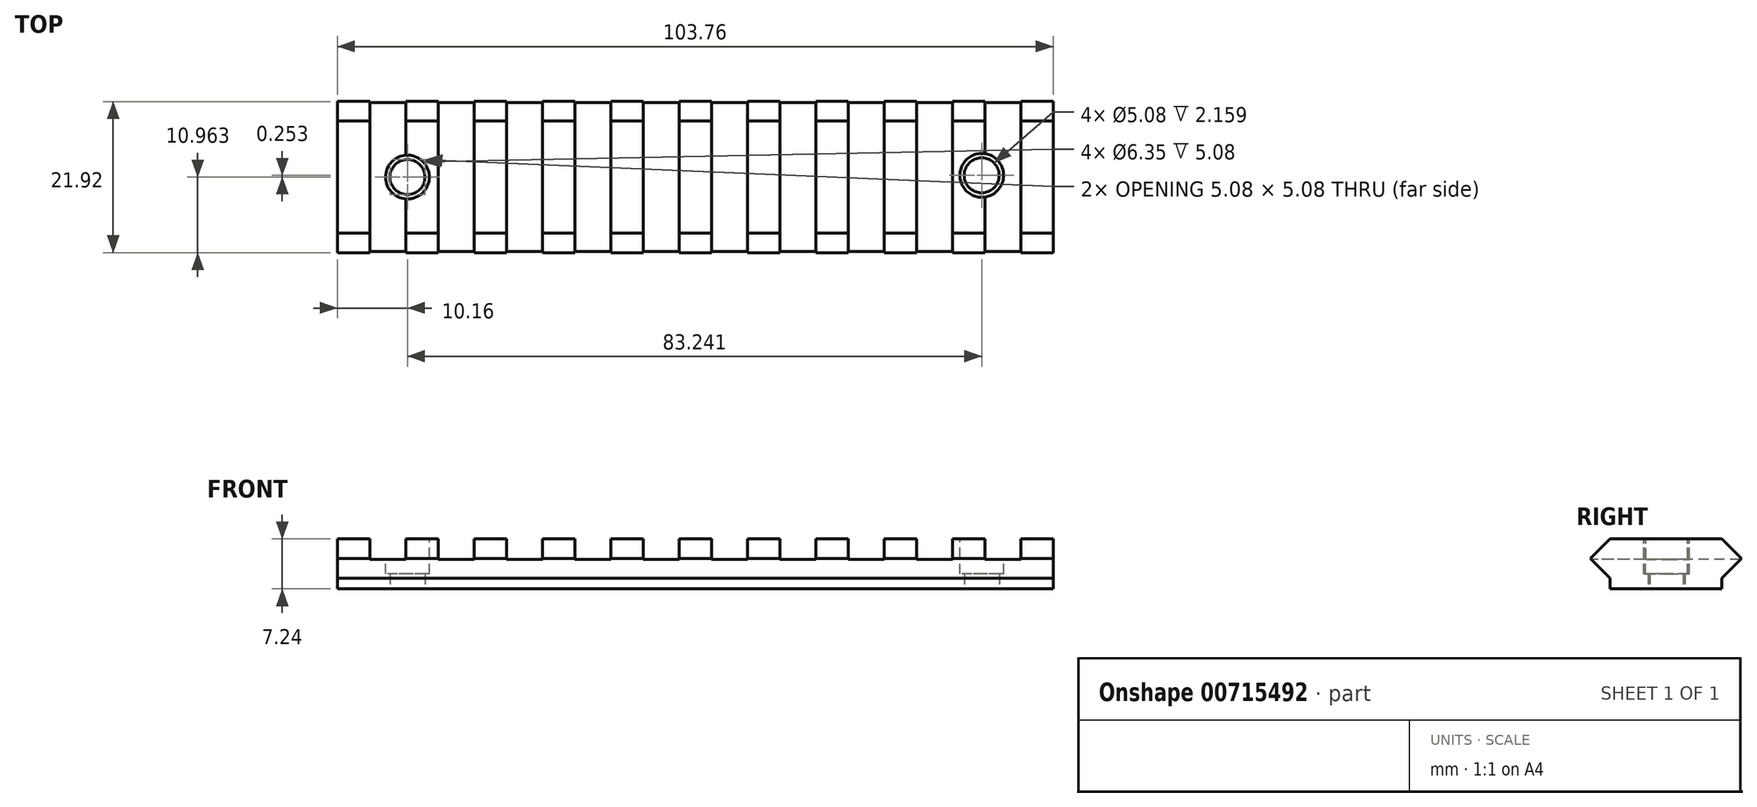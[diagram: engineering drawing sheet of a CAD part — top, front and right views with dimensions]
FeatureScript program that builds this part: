
annotation { "Feature Type Name" : "Feature", "Feature Type Description" : "" }
export const myFeature = defineFeature(function(context is Context, id is Id, definition is map)
    precondition{}
    {
        {
            var Q0;
            Q0=qCreatedBy(makeId("Right.planeOp"),FACE);
            var sketch = newSketch(context, id + "F0", { "sketchPlane" : qUnion([Q0])});
            skLineSegment(sketch, "E0", {"start": v(0, 0) * mm, "end": v(0, 1.52) * mm});
            skLineSegment(sketch, "E1", {"start": v(0, 1.52) * mm, "end": v(-2.86, 4.38) * mm});
            skLineSegment(sketch, "E2", {"start": v(-2.86, 4.38) * mm, "end": v(0, 7.24) * mm});
            skLineSegment(sketch, "E3", {"start": v(0, 7.24) * mm, "end": v(16.2, 7.24) * mm});
            skLineSegment(sketch, "E4", {"start": v(0, 0) * mm, "end": v(16.2, 0) * mm});
            skLineSegment(sketch, "E5", {"start": v(16.2, 0) * mm, "end": v(16.2, 1.52) * mm});
            skLineSegment(sketch, "E6", {"start": v(16.2, 1.52) * mm, "end": v(19.06, 4.38) * mm});
            skLineSegment(sketch, "E7", {"start": v(19.06, 4.38) * mm, "end": v(16.2, 7.24) * mm});
            skSolve(sketch);
        }
        {
            var Q0;
            Q0=makeQuery(id+"F0.imprint","IMPRINT",FACE,{"disambiguationData":[TD([[makeQuery(id+"F0.imprint","IMPRINT",EDGE,{"derivedFrom":sQuery(id+"F0.wireOp",EDGE,"E0")}),-1.0]])]});
            extrude(context, id + "F1", {"entities" : qUnion([Q0]), "depth" : 103.76 * mm});
        }
        {
            var Q0;
            Q0=makeQuery(id+"F1.opExtrude","SWEPT_FACE",FACE,{"disambiguationData":[OSD([sQuery(id+"F0.wireOp",EDGE,"E3")])]});
            var sketch = newSketch(context, id + "F2", { "sketchPlane" : qUnion([Q0])});
            skLineSegment(sketch, "E8", {"start": v(0, 8.1) * mm, "end": v(4.7, 8.1) * mm, "construction": true});
            skLineSegment(sketch, "E9", {"start": v(4.7, 8.1) * mm, "end": v(4.7, 19.06) * mm});
            skLineSegment(sketch, "E10", {"start": v(4.7, 8.1) * mm, "end": v(4.7, -2.86) * mm});
            skLineSegment(sketch, "E11", {"start": v(4.7, 8.1) * mm, "end": v(9.9, 8.1) * mm, "construction": true});
            skLineSegment(sketch, "E12", {"start": v(4.7, 19.06) * mm, "end": v(9.9, 19.06) * mm});
            skLineSegment(sketch, "E13", {"start": v(9.9, 19.06) * mm, "end": v(9.9, -2.86) * mm});
            skLineSegment(sketch, "E14", {"start": v(4.7, -2.86) * mm, "end": v(9.9, -2.86) * mm});
            skLineSegment(sketch, "E15", {"start": v(9.9, 8.1) * mm, "end": v(14.6, 8.1) * mm, "construction": true});
            skLineSegment(sketch, "E16.bottom", {"start": v(14.6, 19.06) * mm, "end": v(19.81, 19.06) * mm});
            skLineSegment(sketch, "E16.top", {"start": v(14.6, -2.86) * mm, "end": v(19.81, -2.86) * mm});
            skLineSegment(sketch, "E16.left", {"start": v(14.6, 19.06) * mm, "end": v(14.6, -2.86) * mm});
            skLineSegment(sketch, "E16.right", {"start": v(19.81, 19.06) * mm, "end": v(19.81, -2.86) * mm});
            skLineSegment(sketch, "E17", {"start": v(19.81, 8.1) * mm, "end": v(24.51, 8.1) * mm, "construction": true});
            skLineSegment(sketch, "E18.bottom", {"start": v(24.51, 19.06) * mm, "end": v(29.72, 19.06) * mm});
            skLineSegment(sketch, "E18.top", {"start": v(24.51, -2.86) * mm, "end": v(29.72, -2.86) * mm});
            skLineSegment(sketch, "E18.left", {"start": v(24.51, 19.06) * mm, "end": v(24.51, -2.86) * mm});
            skLineSegment(sketch, "E18.right", {"start": v(29.72, 19.06) * mm, "end": v(29.72, -2.86) * mm});
            skLineSegment(sketch, "E19.bottom", {"start": v(34.42, 19.06) * mm, "end": v(39.62, 19.06) * mm});
            skLineSegment(sketch, "E19.top", {"start": v(34.42, -2.86) * mm, "end": v(39.62, -2.86) * mm});
            skLineSegment(sketch, "E19.left", {"start": v(34.42, 19.06) * mm, "end": v(34.42, -2.86) * mm});
            skLineSegment(sketch, "E19.right", {"start": v(39.62, 19.06) * mm, "end": v(39.62, -2.86) * mm});
            skLineSegment(sketch, "E20", {"start": v(39.62, 8.1) * mm, "end": v(44.32, 8.1) * mm, "construction": true});
            skLineSegment(sketch, "E21.bottom", {"start": v(44.32, 19.06) * mm, "end": v(49.53, 19.06) * mm});
            skLineSegment(sketch, "E21.top", {"start": v(44.32, -2.86) * mm, "end": v(49.53, -2.86) * mm});
            skLineSegment(sketch, "E21.left", {"start": v(44.32, 19.06) * mm, "end": v(44.32, -2.86) * mm});
            skLineSegment(sketch, "E21.right", {"start": v(49.53, 19.06) * mm, "end": v(49.53, -2.86) * mm});
            skLineSegment(sketch, "E22", {"start": v(49.53, 8.1) * mm, "end": v(54.23, 8.1) * mm, "construction": true});
            skLineSegment(sketch, "E23.bottom", {"start": v(54.23, 19.06) * mm, "end": v(59.44, 19.06) * mm});
            skLineSegment(sketch, "E23.top", {"start": v(54.23, -2.86) * mm, "end": v(59.44, -2.86) * mm});
            skLineSegment(sketch, "E23.left", {"start": v(54.23, 19.06) * mm, "end": v(54.23, -2.86) * mm});
            skLineSegment(sketch, "E23.right", {"start": v(59.44, 19.06) * mm, "end": v(59.44, -2.86) * mm});
            skLineSegment(sketch, "E24", {"start": v(59.44, 8.1) * mm, "end": v(64.13, 8.1) * mm, "construction": true});
            skLineSegment(sketch, "E25.bottom", {"start": v(64.13, 19.06) * mm, "end": v(69.34, 19.06) * mm});
            skLineSegment(sketch, "E25.top", {"start": v(64.13, -2.86) * mm, "end": v(69.34, -2.86) * mm});
            skLineSegment(sketch, "E25.left", {"start": v(64.13, 19.06) * mm, "end": v(64.13, -2.86) * mm});
            skLineSegment(sketch, "E25.right", {"start": v(69.34, 19.06) * mm, "end": v(69.34, -2.86) * mm});
            skLineSegment(sketch, "E26", {"start": v(69.34, 8.1) * mm, "end": v(74.04, 8.1) * mm, "construction": true});
            skLineSegment(sketch, "E27", {"start": v(29.72, 8.1) * mm, "end": v(34.42, 8.1) * mm, "construction": true});
            skLineSegment(sketch, "E28.bottom", {"start": v(74.04, 19.06) * mm, "end": v(79.25, 19.06) * mm});
            skLineSegment(sketch, "E28.top", {"start": v(74.04, -2.86) * mm, "end": v(79.25, -2.86) * mm});
            skLineSegment(sketch, "E28.left", {"start": v(74.04, 19.06) * mm, "end": v(74.04, -2.86) * mm});
            skLineSegment(sketch, "E28.right", {"start": v(79.25, 19.06) * mm, "end": v(79.25, -2.86) * mm});
            skLineSegment(sketch, "E29", {"start": v(79.25, 8.1) * mm, "end": v(83.95, 8.1) * mm, "construction": true});
            skLineSegment(sketch, "E30.bottom", {"start": v(83.95, 19.06) * mm, "end": v(89.15, 19.06) * mm});
            skLineSegment(sketch, "E30.top", {"start": v(83.95, -2.86) * mm, "end": v(89.15, -2.86) * mm});
            skLineSegment(sketch, "E30.left", {"start": v(83.95, 19.06) * mm, "end": v(83.95, -2.86) * mm});
            skLineSegment(sketch, "E30.right", {"start": v(89.15, 19.06) * mm, "end": v(89.15, -2.86) * mm});
            skLineSegment(sketch, "E31", {"start": v(89.15, 8.1) * mm, "end": v(93.85, 8.1) * mm, "construction": true});
            skLineSegment(sketch, "E32.bottom", {"start": v(93.85, 19.15) * mm, "end": v(99.06, 19.15) * mm});
            skLineSegment(sketch, "E32.top", {"start": v(93.85, -2.94) * mm, "end": v(99.06, -2.94) * mm});
            skLineSegment(sketch, "E32.left", {"start": v(93.85, 19.15) * mm, "end": v(93.85, -2.94) * mm});
            skLineSegment(sketch, "E32.right", {"start": v(99.06, 19.15) * mm, "end": v(99.06, -2.94) * mm});
            skSolve(sketch);
        }
        {
            var Q0;
            {var subQ0=sQuery(id+"F2.wireOp",EDGE,"E14");Q0=makeQuery(id+"F2.imprint","IMPRINT",FACE,{"disambiguationData":[TD([[makeQuery(id+"F2.imprint","IMPRINT",EDGE,{"derivedFrom":subQ0}),1.0]])]});}
            var Q1;
            {var subQ0=sQuery(id+"F2.wireOp",EDGE,"E10");var subQ8=sQuery(id+"F2.wireOp",EDGE,"E9");var subQ9=makeQuery(id+"F2.imprint","INTERSECT",VERTEX,{"derivedFrom":[subQ8,subQ0]});Q1=makeQuery(id+"F2.imprint","IMPRINT",FACE,{"disambiguationData":[TD([[makeQuery(id+"F2.imprint","IMPRINT",EDGE,{"disambiguationData":[TD([[subQ9,-1.0]])],"derivedFrom":subQ8}),-1.0]])]});}
            var Q2;
            {var subQ0=sQuery(id+"F2.wireOp",EDGE,"E12");Q2=makeQuery(id+"F2.imprint","IMPRINT",FACE,{"disambiguationData":[TD([[makeQuery(id+"F2.imprint","IMPRINT",EDGE,{"derivedFrom":subQ0}),-1.0]])]});}
            var Q3;
            {var subQ0=sQuery(id+"F2.wireOp",EDGE,"E16.bottom");Q3=makeQuery(id+"F2.imprint","IMPRINT",FACE,{"disambiguationData":[TD([[makeQuery(id+"F2.imprint","IMPRINT",EDGE,{"derivedFrom":subQ0}),-1.0]])]});}
            var Q4;
            {var subQ0=sQuery(id+"F2.wireOp",EDGE,"E16.left");var subQ1=sQuery(id+"F0.wireOp",EDGE,"E3");var subQ2=makeQuery(id+"F1.opExtrude","SWEPT_EDGE",EDGE,{"disambiguationData":[OSD([subQ1,sQuery(id+"F0.wireOp",EDGE,"E7")])]});var subQ3=makeQuery(id+"F2.imprint","INTERSECT",VERTEX,{"derivedFrom":[subQ2,subQ0]});Q4=makeQuery(id+"F2.imprint","IMPRINT",FACE,{"disambiguationData":[TD([[makeQuery(id+"F2.imprint","IMPRINT",EDGE,{"disambiguationData":[TD([[subQ3,-1.0]])],"derivedFrom":subQ0}),1.0]])]});}
            var Q5;
            {var subQ0=sQuery(id+"F2.wireOp",EDGE,"E16.top");Q5=makeQuery(id+"F2.imprint","IMPRINT",FACE,{"disambiguationData":[TD([[makeQuery(id+"F2.imprint","IMPRINT",EDGE,{"derivedFrom":subQ0}),1.0]])]});}
            var Q6;
            {var subQ0=sQuery(id+"F2.wireOp",EDGE,"E18.bottom");Q6=makeQuery(id+"F2.imprint","IMPRINT",FACE,{"disambiguationData":[TD([[makeQuery(id+"F2.imprint","IMPRINT",EDGE,{"derivedFrom":subQ0}),-1.0]])]});}
            var Q7;
            {var subQ0=sQuery(id+"F2.wireOp",EDGE,"E18.left");var subQ1=sQuery(id+"F0.wireOp",EDGE,"E3");var subQ2=makeQuery(id+"F1.opExtrude","SWEPT_EDGE",EDGE,{"disambiguationData":[OSD([subQ1,sQuery(id+"F0.wireOp",EDGE,"E7")])]});var subQ3=makeQuery(id+"F2.imprint","INTERSECT",VERTEX,{"derivedFrom":[subQ2,subQ0]});Q7=makeQuery(id+"F2.imprint","IMPRINT",FACE,{"disambiguationData":[TD([[makeQuery(id+"F2.imprint","IMPRINT",EDGE,{"disambiguationData":[TD([[subQ3,-1.0]])],"derivedFrom":subQ0}),1.0]])]});}
            var Q8;
            {var subQ0=sQuery(id+"F2.wireOp",EDGE,"E18.top");Q8=makeQuery(id+"F2.imprint","IMPRINT",FACE,{"disambiguationData":[TD([[makeQuery(id+"F2.imprint","IMPRINT",EDGE,{"derivedFrom":subQ0}),1.0]])]});}
            var Q9;
            {var subQ0=sQuery(id+"F2.wireOp",EDGE,"E19.bottom");Q9=makeQuery(id+"F2.imprint","IMPRINT",FACE,{"disambiguationData":[TD([[makeQuery(id+"F2.imprint","IMPRINT",EDGE,{"derivedFrom":subQ0}),-1.0]])]});}
            var Q10;
            {var subQ0=sQuery(id+"F2.wireOp",EDGE,"E19.left");var subQ1=sQuery(id+"F0.wireOp",EDGE,"E3");var subQ2=makeQuery(id+"F1.opExtrude","SWEPT_EDGE",EDGE,{"disambiguationData":[OSD([subQ1,sQuery(id+"F0.wireOp",EDGE,"E7")])]});var subQ3=makeQuery(id+"F2.imprint","INTERSECT",VERTEX,{"derivedFrom":[subQ2,subQ0]});Q10=makeQuery(id+"F2.imprint","IMPRINT",FACE,{"disambiguationData":[TD([[makeQuery(id+"F2.imprint","IMPRINT",EDGE,{"disambiguationData":[TD([[subQ3,-1.0]])],"derivedFrom":subQ0}),1.0]])]});}
            var Q11;
            {var subQ0=sQuery(id+"F2.wireOp",EDGE,"E19.top");Q11=makeQuery(id+"F2.imprint","IMPRINT",FACE,{"disambiguationData":[TD([[makeQuery(id+"F2.imprint","IMPRINT",EDGE,{"derivedFrom":subQ0}),1.0]])]});}
            var Q12;
            {var subQ0=sQuery(id+"F2.wireOp",EDGE,"E21.bottom");Q12=makeQuery(id+"F2.imprint","IMPRINT",FACE,{"disambiguationData":[TD([[makeQuery(id+"F2.imprint","IMPRINT",EDGE,{"derivedFrom":subQ0}),-1.0]])]});}
            var Q13;
            {var subQ0=sQuery(id+"F2.wireOp",EDGE,"E21.left");var subQ1=sQuery(id+"F0.wireOp",EDGE,"E3");var subQ2=makeQuery(id+"F1.opExtrude","SWEPT_EDGE",EDGE,{"disambiguationData":[OSD([subQ1,sQuery(id+"F0.wireOp",EDGE,"E7")])]});var subQ3=makeQuery(id+"F2.imprint","INTERSECT",VERTEX,{"derivedFrom":[subQ2,subQ0]});Q13=makeQuery(id+"F2.imprint","IMPRINT",FACE,{"disambiguationData":[TD([[makeQuery(id+"F2.imprint","IMPRINT",EDGE,{"disambiguationData":[TD([[subQ3,-1.0]])],"derivedFrom":subQ0}),1.0]])]});}
            var Q14;
            {var subQ0=sQuery(id+"F2.wireOp",EDGE,"E21.top");Q14=makeQuery(id+"F2.imprint","IMPRINT",FACE,{"disambiguationData":[TD([[makeQuery(id+"F2.imprint","IMPRINT",EDGE,{"derivedFrom":subQ0}),1.0]])]});}
            var Q15;
            {var subQ0=sQuery(id+"F2.wireOp",EDGE,"E23.bottom");Q15=makeQuery(id+"F2.imprint","IMPRINT",FACE,{"disambiguationData":[TD([[makeQuery(id+"F2.imprint","IMPRINT",EDGE,{"derivedFrom":subQ0}),-1.0]])]});}
            var Q16;
            {var subQ0=sQuery(id+"F2.wireOp",EDGE,"E23.left");var subQ1=sQuery(id+"F0.wireOp",EDGE,"E3");var subQ2=makeQuery(id+"F1.opExtrude","SWEPT_EDGE",EDGE,{"disambiguationData":[OSD([subQ1,sQuery(id+"F0.wireOp",EDGE,"E7")])]});var subQ3=makeQuery(id+"F2.imprint","INTERSECT",VERTEX,{"derivedFrom":[subQ2,subQ0]});Q16=makeQuery(id+"F2.imprint","IMPRINT",FACE,{"disambiguationData":[TD([[makeQuery(id+"F2.imprint","IMPRINT",EDGE,{"disambiguationData":[TD([[subQ3,-1.0]])],"derivedFrom":subQ0}),1.0]])]});}
            var Q17;
            {var subQ0=sQuery(id+"F2.wireOp",EDGE,"E23.top");Q17=makeQuery(id+"F2.imprint","IMPRINT",FACE,{"disambiguationData":[TD([[makeQuery(id+"F2.imprint","IMPRINT",EDGE,{"derivedFrom":subQ0}),1.0]])]});}
            var Q18;
            {var subQ0=sQuery(id+"F2.wireOp",EDGE,"E25.bottom");Q18=makeQuery(id+"F2.imprint","IMPRINT",FACE,{"disambiguationData":[TD([[makeQuery(id+"F2.imprint","IMPRINT",EDGE,{"derivedFrom":subQ0}),-1.0]])]});}
            var Q19;
            {var subQ0=sQuery(id+"F2.wireOp",EDGE,"E25.left");var subQ1=sQuery(id+"F0.wireOp",EDGE,"E3");var subQ2=makeQuery(id+"F1.opExtrude","SWEPT_EDGE",EDGE,{"disambiguationData":[OSD([subQ1,sQuery(id+"F0.wireOp",EDGE,"E7")])]});var subQ3=makeQuery(id+"F2.imprint","INTERSECT",VERTEX,{"derivedFrom":[subQ2,subQ0]});Q19=makeQuery(id+"F2.imprint","IMPRINT",FACE,{"disambiguationData":[TD([[makeQuery(id+"F2.imprint","IMPRINT",EDGE,{"disambiguationData":[TD([[subQ3,-1.0]])],"derivedFrom":subQ0}),1.0]])]});}
            var Q20;
            {var subQ0=sQuery(id+"F2.wireOp",EDGE,"E25.top");Q20=makeQuery(id+"F2.imprint","IMPRINT",FACE,{"disambiguationData":[TD([[makeQuery(id+"F2.imprint","IMPRINT",EDGE,{"derivedFrom":subQ0}),1.0]])]});}
            var Q21;
            {var subQ0=sQuery(id+"F2.wireOp",EDGE,"E28.bottom");Q21=makeQuery(id+"F2.imprint","IMPRINT",FACE,{"disambiguationData":[TD([[makeQuery(id+"F2.imprint","IMPRINT",EDGE,{"derivedFrom":subQ0}),-1.0]])]});}
            var Q22;
            {var subQ0=sQuery(id+"F2.wireOp",EDGE,"E28.left");var subQ1=sQuery(id+"F0.wireOp",EDGE,"E3");var subQ2=makeQuery(id+"F1.opExtrude","SWEPT_EDGE",EDGE,{"disambiguationData":[OSD([subQ1,sQuery(id+"F0.wireOp",EDGE,"E7")])]});var subQ3=makeQuery(id+"F2.imprint","INTERSECT",VERTEX,{"derivedFrom":[subQ2,subQ0]});Q22=makeQuery(id+"F2.imprint","IMPRINT",FACE,{"disambiguationData":[TD([[makeQuery(id+"F2.imprint","IMPRINT",EDGE,{"disambiguationData":[TD([[subQ3,-1.0]])],"derivedFrom":subQ0}),1.0]])]});}
            var Q23;
            {var subQ0=sQuery(id+"F2.wireOp",EDGE,"E28.top");Q23=makeQuery(id+"F2.imprint","IMPRINT",FACE,{"disambiguationData":[TD([[makeQuery(id+"F2.imprint","IMPRINT",EDGE,{"derivedFrom":subQ0}),1.0]])]});}
            var Q24;
            {var subQ0=sQuery(id+"F2.wireOp",EDGE,"E30.top");Q24=makeQuery(id+"F2.imprint","IMPRINT",FACE,{"disambiguationData":[TD([[makeQuery(id+"F2.imprint","IMPRINT",EDGE,{"derivedFrom":subQ0}),1.0]])]});}
            var Q25;
            {var subQ0=sQuery(id+"F2.wireOp",EDGE,"E30.left");var subQ1=sQuery(id+"F0.wireOp",EDGE,"E3");var subQ2=makeQuery(id+"F1.opExtrude","SWEPT_EDGE",EDGE,{"disambiguationData":[OSD([subQ1,sQuery(id+"F0.wireOp",EDGE,"E7")])]});var subQ3=makeQuery(id+"F2.imprint","INTERSECT",VERTEX,{"derivedFrom":[subQ2,subQ0]});Q25=makeQuery(id+"F2.imprint","IMPRINT",FACE,{"disambiguationData":[TD([[makeQuery(id+"F2.imprint","IMPRINT",EDGE,{"disambiguationData":[TD([[subQ3,-1.0]])],"derivedFrom":subQ0}),1.0]])]});}
            var Q26;
            {var subQ0=sQuery(id+"F2.wireOp",EDGE,"E30.bottom");Q26=makeQuery(id+"F2.imprint","IMPRINT",FACE,{"disambiguationData":[TD([[makeQuery(id+"F2.imprint","IMPRINT",EDGE,{"derivedFrom":subQ0}),-1.0]])]});}
            var Q27;
            {var subQ0=sQuery(id+"F2.wireOp",EDGE,"E32.bottom");Q27=makeQuery(id+"F2.imprint","IMPRINT",FACE,{"disambiguationData":[TD([[makeQuery(id+"F2.imprint","IMPRINT",EDGE,{"derivedFrom":subQ0}),-1.0]])]});}
            var Q28;
            {var subQ0=sQuery(id+"F2.wireOp",EDGE,"E32.left");var subQ1=sQuery(id+"F0.wireOp",EDGE,"E3");var subQ2=makeQuery(id+"F1.opExtrude","SWEPT_EDGE",EDGE,{"disambiguationData":[OSD([subQ1,sQuery(id+"F0.wireOp",EDGE,"E7")])]});var subQ3=makeQuery(id+"F2.imprint","INTERSECT",VERTEX,{"derivedFrom":[subQ2,subQ0]});Q28=makeQuery(id+"F2.imprint","IMPRINT",FACE,{"disambiguationData":[TD([[makeQuery(id+"F2.imprint","IMPRINT",EDGE,{"disambiguationData":[TD([[subQ3,-1.0]])],"derivedFrom":subQ0}),1.0]])]});}
            var Q29;
            {var subQ0=sQuery(id+"F2.wireOp",EDGE,"E32.top");Q29=makeQuery(id+"F2.imprint","IMPRINT",FACE,{"disambiguationData":[TD([[makeQuery(id+"F2.imprint","IMPRINT",EDGE,{"derivedFrom":subQ0}),1.0]])]});}
            extrude(context, id + "F3", {"entities" : qUnion([Q0, Q1, Q2, Q3, Q4, Q5, Q6, Q7, Q8, Q9, Q10, Q11, Q12, Q13, Q14, Q15, Q16, Q17, Q18, Q19, Q20, Q21, Q22, Q23, Q24, Q25, Q26, Q27, Q28, Q29]), "operationType" : NewBodyOperationType.REMOVE, "oppositeDirection" : true, "depth" : 3 * mm});
        }
        {
            var Q0;
            Q0=makeQuery(id+"F1.opExtrude","SWEPT_FACE",FACE,{"disambiguationData":[OSD([sQuery(id+"F0.wireOp",EDGE,"E4")])]});
            var sketch = newSketch(context, id + "F4", { "sketchPlane" : qUnion([Q0])});
            skCircle(sketch, "E33", {"center": v(93.4, -8.36) * mm, "radius": 2.54 * mm});
            skCircle(sketch, "E34", {"center": v(10.16, -8.1) * mm, "radius": 2.54 * mm});
            skLineSegment(sketch, "E35", {"start": v(10.16, -8.1) * mm, "end": v(0, -8.1) * mm, "construction": true});
            skPoint(sketch, "E35.endSnap0", {"position": v(0, -8.1) * mm});
            skLineSegment(sketch, "E36", {"start": v(93.4, -8.36) * mm, "end": v(10.16, -8.1) * mm, "construction": true});
            skSolve(sketch);
        }
        {
            var Q0;
            Q0=makeQuery(id+"F4.imprint","IMPRINT",FACE,{"disambiguationData":[TD([[makeQuery(id+"F4.imprint","IMPRINT",EDGE,{"derivedFrom":sQuery(id+"F4.wireOp",EDGE,"E33")}),1.0]])]});
            var Q1;
            Q1=makeQuery(id+"F4.imprint","IMPRINT",FACE,{"disambiguationData":[TD([[makeQuery(id+"F4.imprint","IMPRINT",EDGE,{"derivedFrom":sQuery(id+"F4.wireOp",EDGE,"E34")}),1.0]])]});
            extrude(context, id + "F5", {"entities" : qUnion([Q0, Q1]), "operationType" : NewBodyOperationType.REMOVE, "oppositeDirection" : true, "depth" : 7.24 * mm});
        }
        {
            var Q0;
            Q0=makeQuery(id+"F3.boolean.opBoolean","SPLIT",FACE,{"disambiguationData":[TD([makeQuery(id+"F3.opExtrude","SWEPT_FACE",FACE,{"disambiguationData":[OSD([sQuery(id+"F2.wireOp",EDGE,"E18.right")])]})])],"derivedFrom":makeQuery(id+"F1.opExtrude","SWEPT_FACE",FACE,{"disambiguationData":[OSD([sQuery(id+"F0.wireOp",EDGE,"E3")])]})});
            var sketch = newSketch(context, id + "F6", { "sketchPlane" : qUnion([Q0])});
            skCircle(sketch, "E37", {"center": v(10.16, 8.1) * mm, "radius": 3.18 * mm});
            skCircle(sketch, "E38", {"center": v(93.4, 8.36) * mm, "radius": 3.18 * mm});
            skCircle(sketch, "E39", {"center": v(10.16, 8.1) * mm, "radius": 2.54 * mm, "construction": true});
            skCircle(sketch, "E40", {"center": v(93.4, 8.36) * mm, "radius": 2.54 * mm, "construction": true});
            skSolve(sketch);
        }
        {
            var Q0;
            Q0=makeQuery(id+"F6.imprint","IMPRINT",FACE,{"disambiguationData":[TD([[makeQuery(id+"F6.imprint","IMPRINT",EDGE,{"derivedFrom":sQuery(id+"F6.wireOp",EDGE,"E38")}),1.0]])]});
            var Q1;
            Q1=makeQuery(id+"F6.imprint","IMPRINT",FACE,{"disambiguationData":[TD([[makeQuery(id+"F6.imprint","IMPRINT",EDGE,{"derivedFrom":sQuery(id+"F6.wireOp",EDGE,"E37")}),1.0]])]});
            extrude(context, id + "F7", {"entities" : qUnion([Q0, Q1]), "operationType" : NewBodyOperationType.REMOVE, "oppositeDirection" : true, "depth" : 5.08 * mm});
        }
        {
            var Q0;
            Q0=makeQuery(id+"F1.opExtrude","SWEPT_BODY",BODY,{"disambiguationData":[OSD([sQuery(id+"F0.wireOp",EDGE,"E0"),sQuery(id+"F0.wireOp",EDGE,"E1"),sQuery(id+"F0.wireOp",EDGE,"E2"),sQuery(id+"F0.wireOp",EDGE,"E3"),sQuery(id+"F0.wireOp",EDGE,"E4"),sQuery(id+"F0.wireOp",EDGE,"E5"),sQuery(id+"F0.wireOp",EDGE,"E6"),sQuery(id+"F0.wireOp",EDGE,"E7")])]});
            transform(context, id + "F8", {"entities" : qUnion([Q0]), "transformType" : TransformType.TRANSLATION_3D, "dx" : 0 * mm, "dy" : 0 * mm, "dz" : 0 * mm, "makeCopy" : true});
        }
    });
